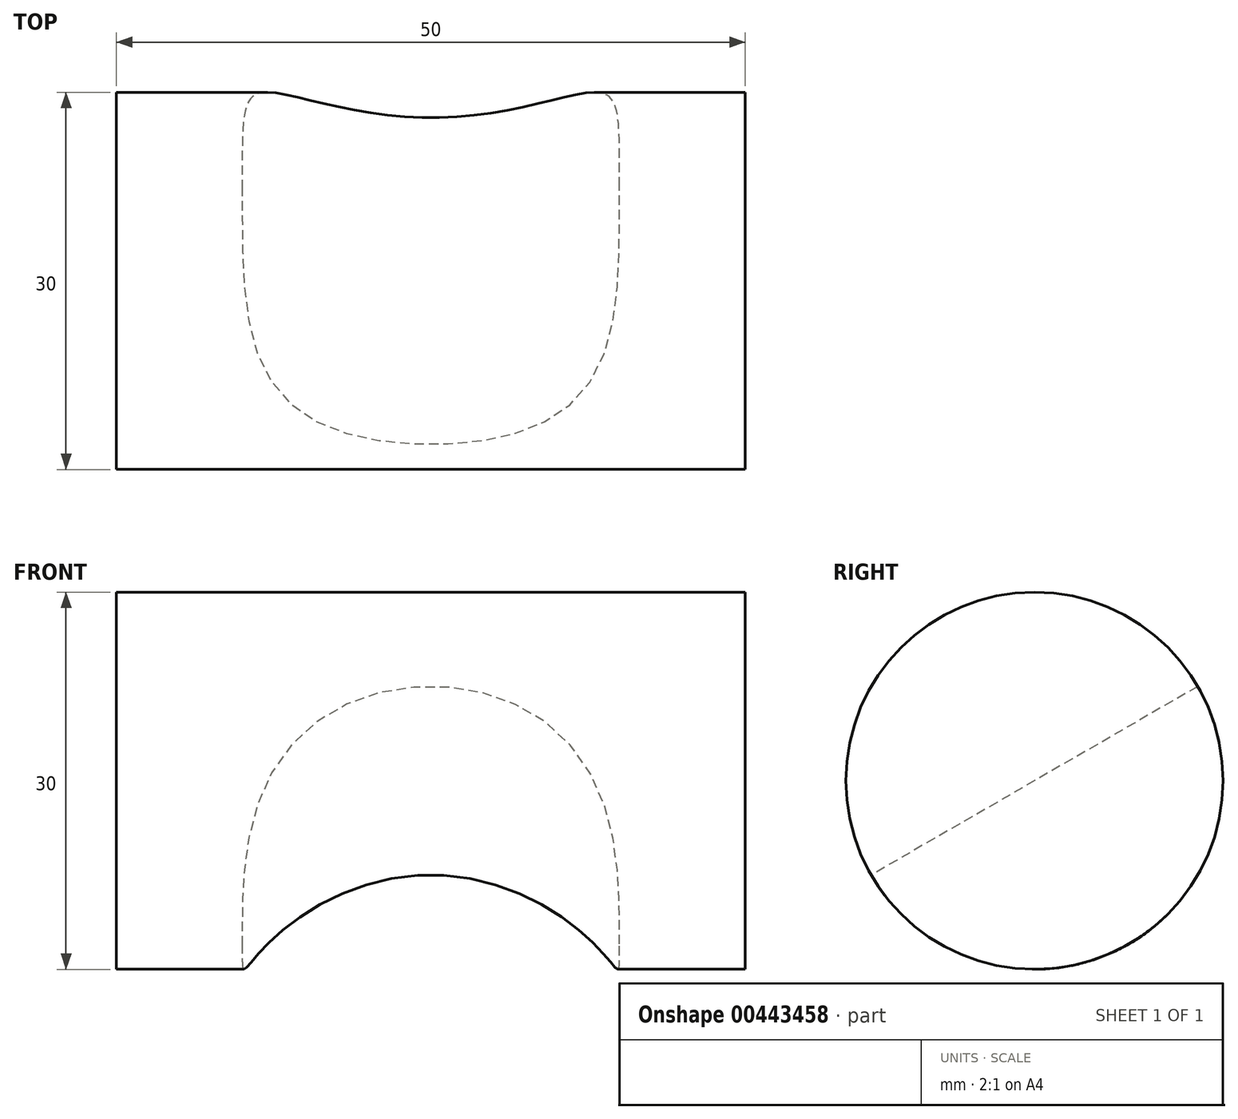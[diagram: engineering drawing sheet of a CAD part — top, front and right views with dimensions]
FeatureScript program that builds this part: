
annotation { "Feature Type Name" : "Feature", "Feature Type Description" : "" }
export const myFeature = defineFeature(function(context is Context, id is Id, definition is map)
    precondition{}
    {
        {
            var Q0;
            Q0=qCreatedBy(makeId("Right.planeOp"),FACE);
            var sketch = newSketch(context, id + "F0", { "sketchPlane" : qUnion([Q0])});
            skCircle(sketch, "E0", {"center": v(0, 0) * mm, "radius": 15 * mm});
            skSolve(sketch);
        }
        {
            var Q0;
            Q0 = qSketchRegion(id + "F0", true);
            extrude(context, id + "F1", {"entities" : qUnion([Q0]), "depth" : 25 * mm, "hasSecondDirection" : true, "secondDirectionOppositeDirection" : true, "secondDirectionDepth" : 25 * mm});
        }
        {
            var Q0;
            Q0=qCreatedBy(makeId("Front.planeOp"),FACE);
            var sketch = newSketch(context, id + "F2", { "sketchPlane" : qUnion([Q0])});
            skCircle(sketch, "E1", {"center": v(0, -15) * mm, "radius": 15 * mm});
            skSolve(sketch);
        }
        {
            var Q0;
            Q0 = qSketchRegion(id + "F2", true);
            extrude(context, id + "F3", {"entities" : qUnion([Q0]), "operationType" : NewBodyOperationType.REMOVE, "oppositeDirection" : true, "depth" : 25 * mm, "hasSecondDirection" : true, "secondDirectionOppositeDirection" : false, "secondDirectionDepth" : 25 * mm});
        }
        {
            var Q0;
            Q0=qCreatedBy(makeId("Top.planeOp"),FACE);
            var sketch = newSketch(context, id + "F4", { "sketchPlane" : qUnion([Q0])});
            skLineSegment(sketch, "E2", {"start": v(0, 0) * mm, "end": v(62.61, 0) * mm});
            skSolve(sketch);
        }
        {
            var Q0;
            Q0=makeQuery(id+"F1.opExtrude","SWEPT_BODY",BODY,{"disambiguationData":[OSD([sQuery(id+"F0.wireOp",EDGE,"E0")])]});
            var Q1;
            Q1=sQuery(id+"F4.wireOp",EDGE,"E2");
            transform(context, id + "F5", {"entities" : qUnion([Q0]), "transformType" : TransformType.ROTATION, "transformAxis" : qUnion([Q1]), "angle" : 30 * degree, "makeCopy" : false});
        }
    });
